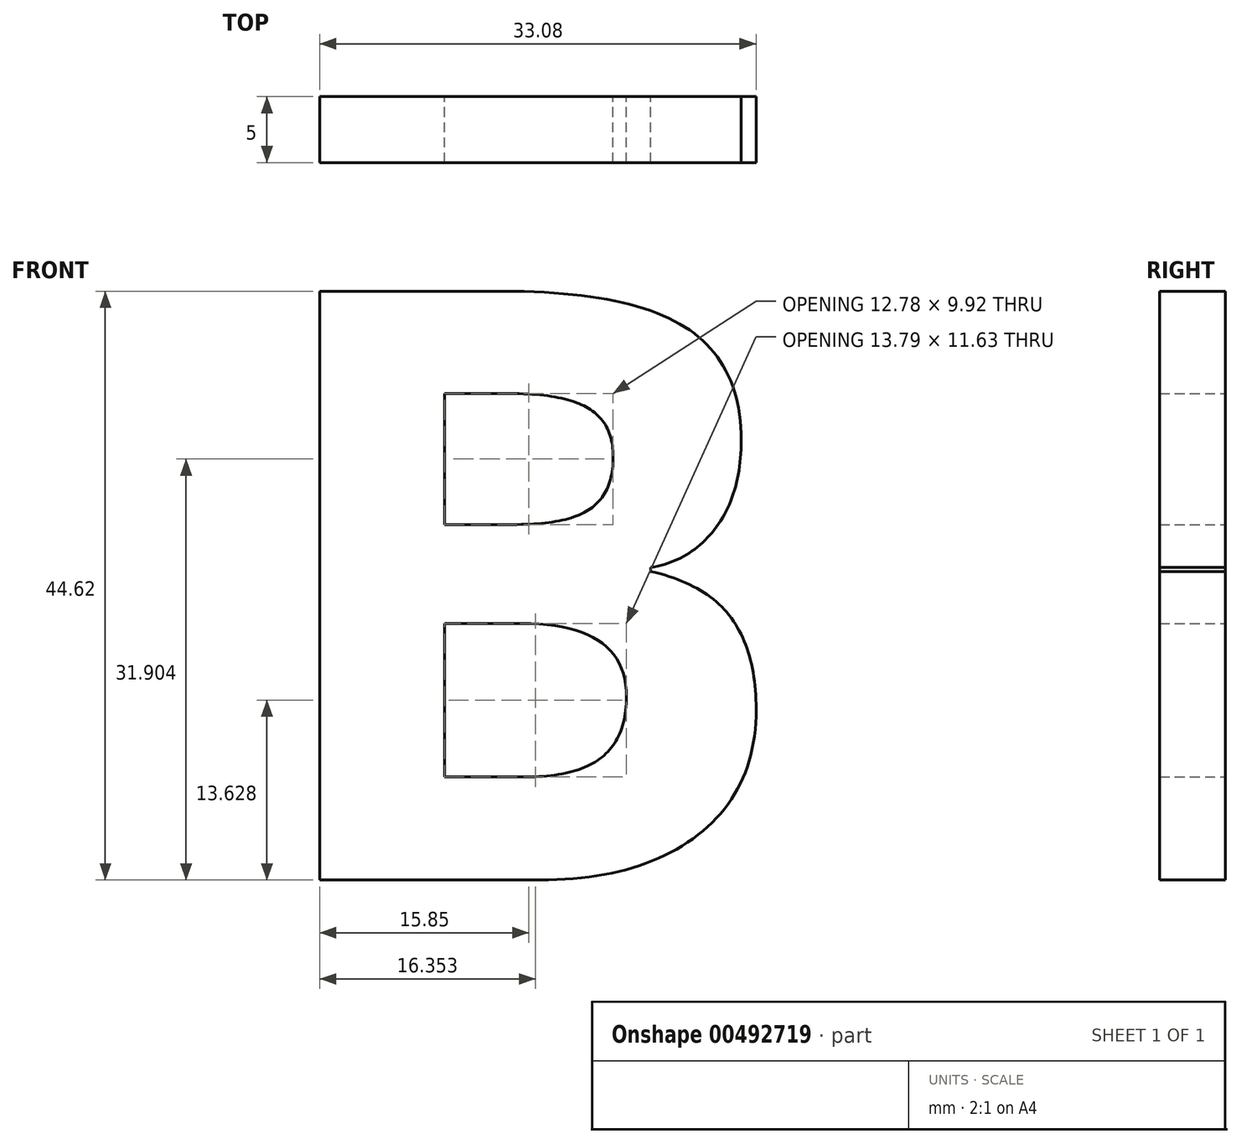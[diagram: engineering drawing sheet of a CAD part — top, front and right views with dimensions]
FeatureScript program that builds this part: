
annotation { "Feature Type Name" : "Feature", "Feature Type Description" : "" }
export const myFeature = defineFeature(function(context is Context, id is Id, definition is map)
    precondition{}
    {
        {
            var Q0;
            Q0=qCreatedBy(makeId("Front.planeOp"),FACE);
            var sketch = newSketch(context, id + "F0", { "sketchPlane" : qUnion([Q0])});
            skText(sketch, "E0", { "text": "B", "fontName": "OpenSans-Bold.ttf"});
            const initialGuessF0  = {"E0": [0.01204, -0.0552, 1, 0, 0.045]};
            skSetInitialGuess(sketch, initialGuessF0);
            skSolve(sketch);
        }
        {
            var Q0;
            Q0=makeQuery(id+"F0.imprint","IMPRINT",FACE,{"disambiguationData":[TD([[makeQuery(id+"F0.imprint","IMPRINT",EDGE,{"derivedFrom":sQuery(id+"F0.wireOp",EDGE,"E0.sketch_text.stroke-0")}),-1.0]])]});
            extrude(context, id + "F1", {"entities" : qUnion([Q0]), "depth" : 5 * mm});
        }
    });
